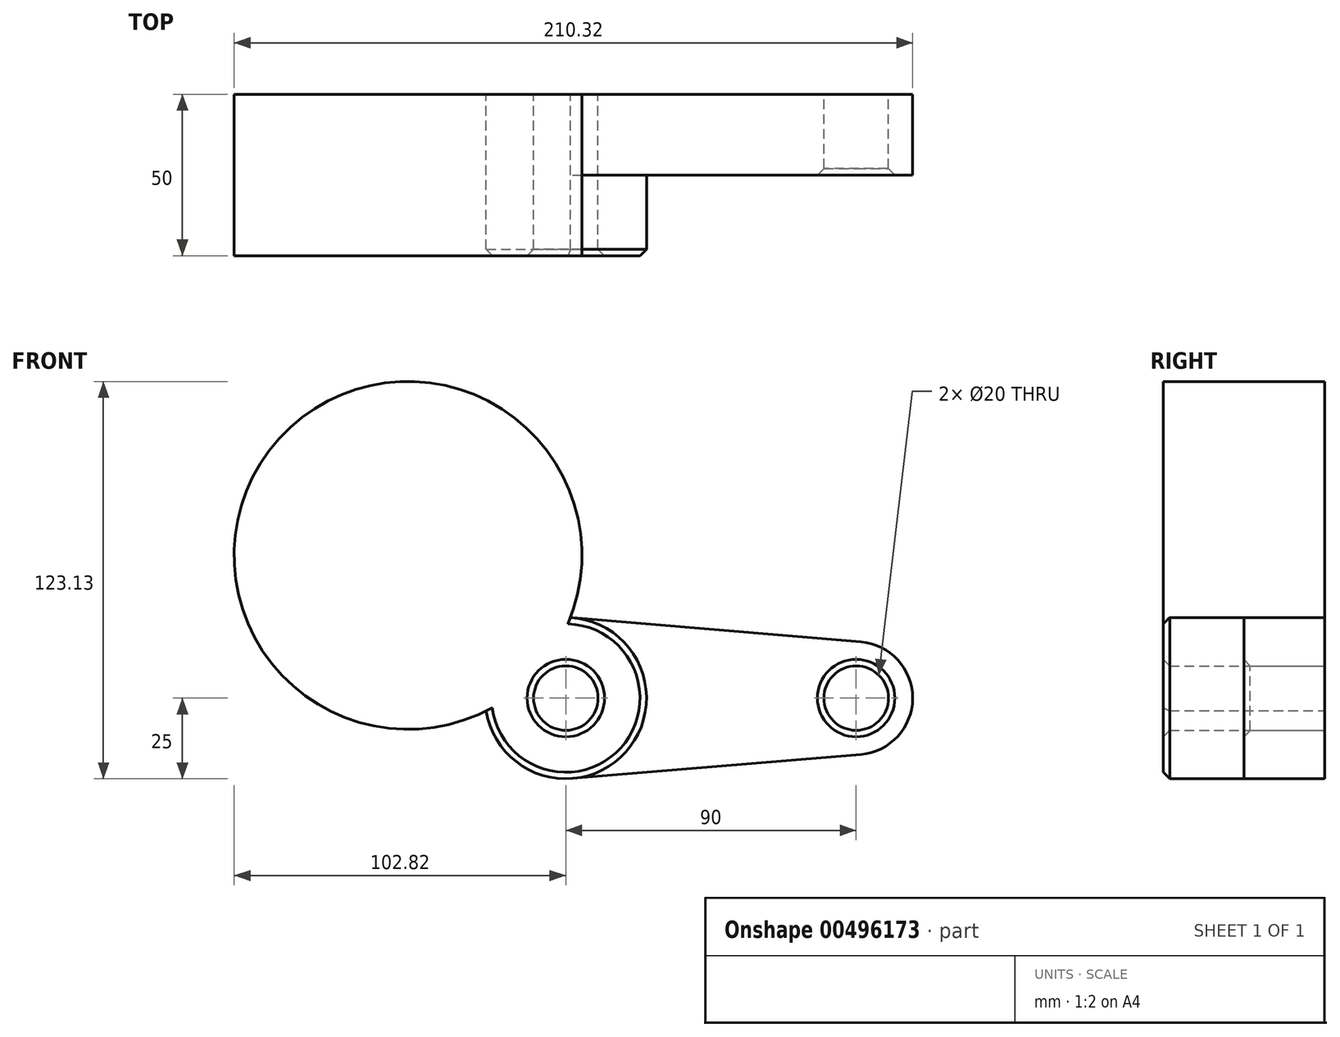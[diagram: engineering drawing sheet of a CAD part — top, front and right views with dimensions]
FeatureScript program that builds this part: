
annotation { "Feature Type Name" : "Feature", "Feature Type Description" : "" }
export const myFeature = defineFeature(function(context is Context, id is Id, definition is map)
    precondition{}
    {
        {
            var Q0;
            Q0=qCreatedBy(makeId("Front.planeOp"),FACE);
            var sketch = newSketch(context, id + "F0", { "sketchPlane" : qUnion([Q0])});
            skCircle(sketch, "E0", {"center": v(0, 0) * mm, "radius": 25 * mm});
            skCircle(sketch, "E1", {"center": v(90, 0) * mm, "radius": 17.5 * mm});
            skLineSegment(sketch, "E2", {"start": v(2.08, 24.91) * mm, "end": v(91.46, 17.44) * mm});
            skLineSegment(sketch, "E3", {"start": v(2.08, -24.91) * mm, "end": v(91.46, -17.44) * mm});
            skCircle(sketch, "E4", {"center": v(0, 0) * mm, "radius": 10 * mm});
            skCircle(sketch, "E5", {"center": v(90, 0) * mm, "radius": 10 * mm});
            skSolve(sketch);
        }
        {
            var Q0;
            Q0=qSketchRegion(id+"F0",true);
            extrude(context, id + "F1", {"entities" : qUnion([Q0]), "depth" : 25 * mm});
        }
        {
            var Q0;
            Q0=makeQuery(id+"F0.imprint","IMPRINT",FACE,{"disambiguationData":[TD([[makeQuery(id+"F0.imprint","IMPRINT",EDGE,{"derivedFrom":sQuery(id+"F0.wireOp",EDGE,"E4")}),-1.0]])]});
            extrude(context, id + "F2", {"entities" : qUnion([Q0]), "operationType" : NewBodyOperationType.ADD, "depth" : 50 * mm});
        }
        {
            var Q0;
            Q0=makeQuery(id+"F2.opExtrude","CAP_EDGE",EDGE,{"disambiguationData":[OSD([sQuery(id+"F0.wireOp",EDGE,"E0")])],"isStart":false});
            var Q1;
            Q1=makeQuery(id+"F2.opExtrude","CAP_EDGE",EDGE,{"disambiguationData":[OSD([sQuery(id+"F0.wireOp",EDGE,"E4")])],"isStart":false});
            var Q2;
            Q2=makeQuery(id+"F1.opExtrude","CAP_EDGE",EDGE,{"disambiguationData":[OSD([sQuery(id+"F0.wireOp",EDGE,"E5")])],"isStart":false});
            chamfer(context, id + "F3", {"entities" : qUnion([Q0, Q1, Q2]), "width" : 2 * mm, "tangentPropagation" : true});
        }
        {
            var Q0;
            Q0=qCreatedBy(makeId("Front.planeOp"),FACE);
            var sketch = newSketch(context, id + "F4", { "sketchPlane" : qUnion([Q0])});
            skCircle(sketch, "E6", {"center": v(-48.91, 44.22) * mm, "radius": 53.91 * mm});
            skSolve(sketch);
        }
        {
            var Q0;
            Q0 = qSketchRegion(id + "F4", true);
            var sketch = newSketch(context, id + "F5", { "sketchPlane" : qUnion([Q0])});
            skSolve(sketch);
        }
        {
            var Q0;
            Q0 = qSketchRegion(id + "F5", true);
            var Q1;
            Q1=makeQuery(id+"F4.imprint","IMPRINT",FACE,{"disambiguationData":[TD([[makeQuery(id+"F4.imprint","IMPRINT",EDGE,{"derivedFrom":sQuery(id+"F4.wireOp",EDGE,"E6")}),1.0]])]});
            extrude(context, id + "F6", {"entities" : qUnion([Q0, Q1]), "operationType" : NewBodyOperationType.ADD, "depth" : 50 * mm});
        }
    });
